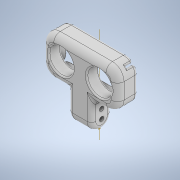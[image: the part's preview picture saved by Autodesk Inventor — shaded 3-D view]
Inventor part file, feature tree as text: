
AUTODESK INVENTOR PART (.ipt)
format: ipt  version: 2021 (Build 250183000, 183)  size: 923,136 bytes
history: native  units: mm
features: fillet x19, extrude x11, sketch x11, other x2
ambient origin geometry x8: Origin, YZ Plane, XZ Plane, XY Plane, X Axis, Y Axis, Z Axis, Center Point
bodies: Body1 (feature_tree), Body2 (feature_tree)
feature tree (43):
  other  "Ping Sensor Base"
  extrude  "Extrusion1"  Depth=3.0mm TaperAngle=0.0deg
  extrude  "Extrusion2"  Depth=3.0mm TaperAngle=0.0deg
  extrude  "Extrusion3"  Depth=1.55mm
  fillet  "Fillet1"  Radius=12.0mm
  extrude  "Extrusion4"  Depth=14.0mm
  extrude  "Extrusion6"  Depth=1.5mm
  fillet  "Fillet9"  Radius=7.0mm
  fillet  "Fillet10"  Radius=7.0mm
  fillet  "Fillet11"  [1 undecoded]
  fillet  "Fillet12"  Radius=15.0mm
  fillet  "Fillet15"  Radius=6.0mm
  fillet  "Fillet16"  Radius=15.0mm
  extrude  "Extrusion7"  Depth=30.0mm
  extrude  "Extrusion8"  Depth=3.1mm
  extrude  "Extrusion9"  Depth=3.0mm
  extrude  "Extrusion10"  Depth=8.2mm
  fillet  "Fillet17"  Radius=10.2mm
  fillet  "Fillet18"  Radius=8.2mm
  fillet  "Fillet19"  Radius=10.2mm
  fillet  "Fillet20"  Radius=7.5mm
  fillet  "Fillet21"  Radius=7.5mm
  fillet  "Fillet22"  [1 undecoded]
  extrude  "Extrusion11"  Depth=7.0mm
  fillet  "Fillet27"  Radius=2.0mm
  extrude  "Extrusion13"  Depth=1.0mm
  fillet  "Fillet29"  Radius=2.0mm
  fillet  "Fillet30"  Radius=3.0mm
  fillet  "Fillet31"  Radius=17.0mm
  fillet  "Fillet32"  Radius=30.0mm
  fillet  "Fillet33"  Radius=10.0mm
  sketch  "Sketch1"  dims[d0=36.0mm d1=3.0mm d2=0.0mm]
  sketch  "Sketch2"  dims[d3=3.1mm d4=3.0mm d5=0.0mm]
  sketch  "Sketch3"  dims[d7=3.1mm d8=1.55mm d9=12.0mm]
  sketch  "Sketch4"  dims[d10=3.0mm d11=0.0mm d15=14.0mm]
  sketch  "Sketch6"  dims[d16=3.5mm d17=1.5mm]
  sketch  "Sketch7"  dims[d18=2.5mm d19=6.5mm d20=20.0mm d21=0.0mm d22=7.0mm d23=7.0mm d24=0.0mm d25=15.0mm d37=6.0mm d54=15.0mm]
  other  "Ping Sensor Housing"
  sketch  "Sketch8"  dims[d55=15.0mm d56=30.0mm]
  sketch  "Sketch9"  dims[d57=3.0mm d58=3.1mm]
  sketch  "Sketch10"  dims[d59=4.5mm d60=3.0mm]
  sketch  "Sketch11"  dims[d61=3.1mm d62=8.2mm d63=10.2mm d64=8.2mm d65=10.2mm d66=7.5mm d67=7.5mm d68=0.0mm d69=0.0mm]
  sketch  "Sketch13"  dims[d70=1.5mm d71=7.0mm d72=2.0mm d73=1.0mm d76=2.0mm d77=3.0mm d78=17.0mm d79=30.0mm d80=10.0mm d81=0.0mm d82=27.0mm d83=26.0mm d84=26.0mm d85=10.0mm d86=0.0mm d87=45.8mm d88=20.8mm d89=3.1mm d90=3.1mm d91=3.1mm d92=3.1mm d93=5.5mm d94=0.0mm d95=17.0mm d96=17.0mm d97=9.75mm d99=9.75mm d100=10.0mm d101=10.0mm d102=9.3mm d103=0.0mm d104=0.0mm d105=8.0mm d106=4.5mm d107=2.0mm d108=7.0mm d109=3.0mm d110=3.0mm d111=3.1mm d112=3.1mm d113=6.1mm d114=0.0mm d115=0.0mm d116=4.0mm d118=4.0mm d135=0.9mm d137=0.0mm d138=6.0mm d139=5.0mm d140=5.0mm d141=4.0mm d142=3.0mm d143=0.0mm d144=1.0mm d145=0.3mm d146=1.0mm d147=26.3mm d148=43.3mm d149=1.0mm d150=1.0mm]
note: 2 required parameter values undecoded (feature->parameter linkage not recoverable at this tier; creation-order binding heuristic only, values carry confidence <= 0.55)
